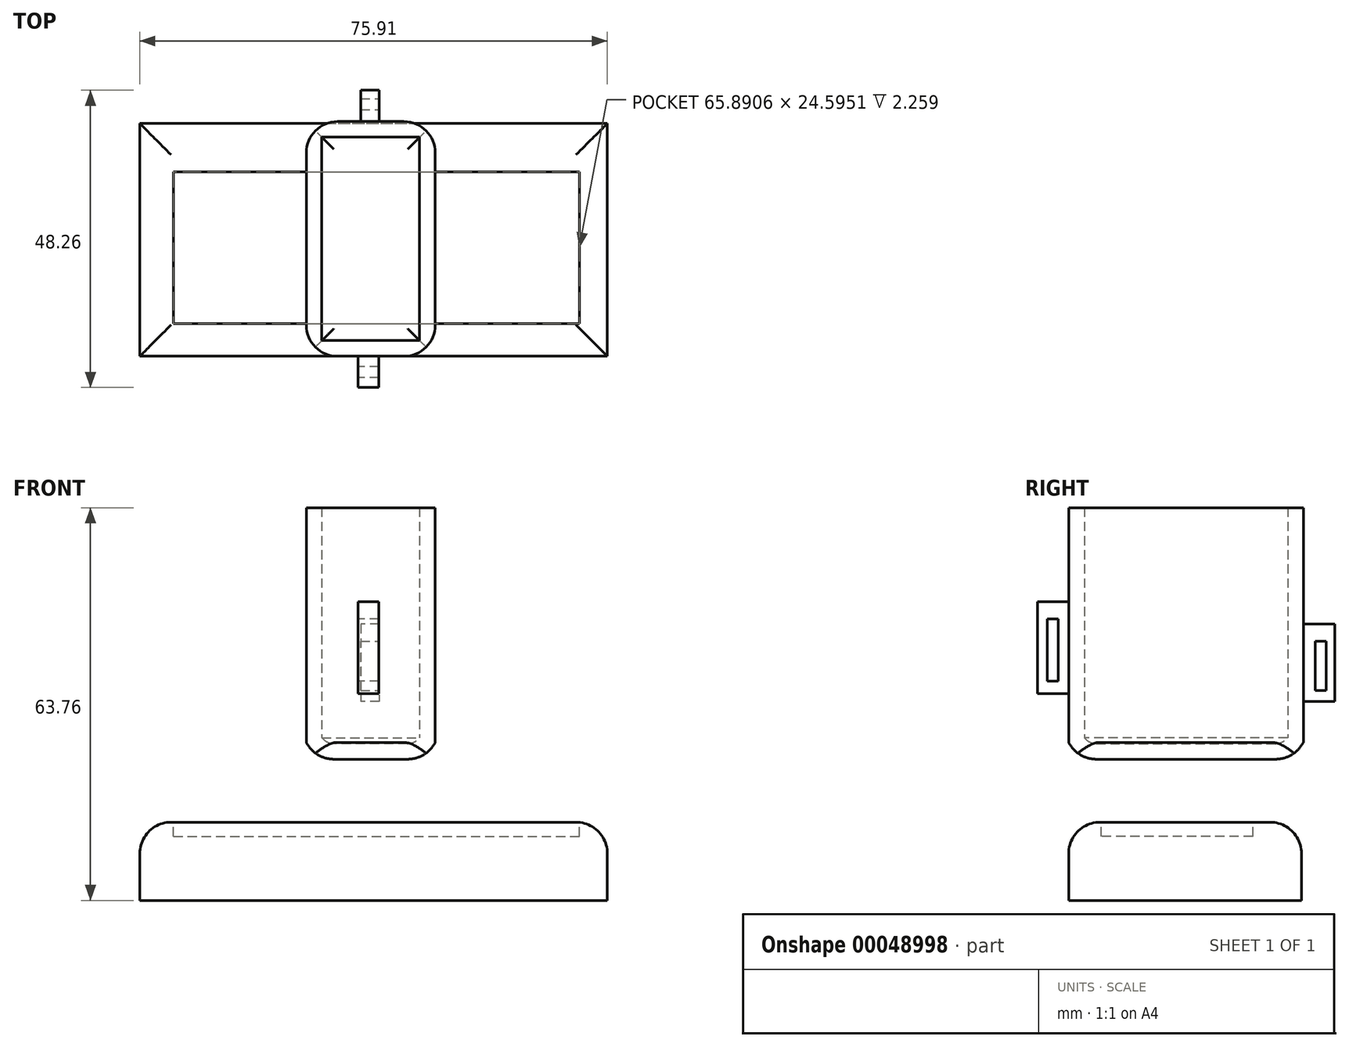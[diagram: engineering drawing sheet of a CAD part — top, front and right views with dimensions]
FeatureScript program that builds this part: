
annotation { "Feature Type Name" : "Feature", "Feature Type Description" : "" }
export const myFeature = defineFeature(function(context is Context, id is Id, definition is map)
    precondition{}
    {
        {
            var Q0;
            Q0=qCreatedBy(makeId("Top.planeOp"),FACE);
            var sketch = newSketch(context, id + "F0", { "sketchPlane" : qUnion([Q0])});
            skLineSegment(sketch, "E0.bottom", {"start": v(0, 0) * mm, "end": v(75.91, 0) * mm});
            skLineSegment(sketch, "E0.top", {"start": v(0, 37.8) * mm, "end": v(75.91, 37.8) * mm});
            skLineSegment(sketch, "E0.left", {"start": v(0, 0) * mm, "end": v(0, 37.8) * mm});
            skLineSegment(sketch, "E0.right", {"start": v(75.91, 0) * mm, "end": v(75.91, 37.8) * mm});
            skSolve(sketch);
        }
        {
            var Q0;
            Q0=makeQuery(id+"F0.imprint","IMPRINT",FACE,{"disambiguationData":[TD([[makeQuery(id+"F0.imprint","IMPRINT",EDGE,{"derivedFrom":sQuery(id+"F0.wireOp",EDGE,"E0.bottom")}),1.0]])]});
            extrude(context, id + "F1", {"entities" : qUnion([Q0]), "depth" : 12.7 * mm});
        }
        {
            var Q0;
            Q0=makeQuery(id+"F1.opExtrude","CAP_FACE",FACE,{"disambiguationData":[OSD([sQuery(id+"F0.wireOp",EDGE,"E0.bottom"),sQuery(id+"F0.wireOp",EDGE,"E0.top"),sQuery(id+"F0.wireOp",EDGE,"E0.left"),sQuery(id+"F0.wireOp",EDGE,"E0.right")])],"isStart":false});
            var sketch = newSketch(context, id + "F2", { "sketchPlane" : qUnion([Q0])});
            skLineSegment(sketch, "E1.bottom", {"start": v(5.47, 29.9) * mm, "end": v(71.36, 29.9) * mm});
            skLineSegment(sketch, "E1.top", {"start": v(5.47, 5.31) * mm, "end": v(71.36, 5.31) * mm});
            skLineSegment(sketch, "E1.left", {"start": v(5.47, 29.9) * mm, "end": v(5.47, 5.31) * mm});
            skLineSegment(sketch, "E1.right", {"start": v(71.36, 29.9) * mm, "end": v(71.36, 5.31) * mm});
            skSolve(sketch);
        }
        {
            var Q0;
            Q0=makeQuery(id+"F2.imprint","IMPRINT",FACE,{"disambiguationData":[TD([[makeQuery(id+"F2.imprint","IMPRINT",EDGE,{"derivedFrom":sQuery(id+"F2.wireOp",EDGE,"E1.bottom")}),-1.0]])]});
            extrude(context, id + "F3", {"entities" : qUnion([Q0]), "operationType" : NewBodyOperationType.REMOVE, "oppositeDirection" : true, "depth" : 2.3 * mm});
        }
        {
            var Q0;
            Q0=makeQuery(id+"F3.boolean.opBoolean","COPY",FACE,{"derivedFrom":makeQuery(id+"F3.opExtrude","CAP_FACE",FACE,{"disambiguationData":[OSD([sQuery(id+"F2.wireOp",EDGE,"E1.bottom"),sQuery(id+"F2.wireOp",EDGE,"E1.top"),sQuery(id+"F2.wireOp",EDGE,"E1.left"),sQuery(id+"F2.wireOp",EDGE,"E1.right")])],"isStart":false})});
            var sketch = newSketch(context, id + "F4", { "sketchPlane" : qUnion([Q0])});
            skSolve(sketch);
        }
        {
            var Q0;
            Q0=makeQuery(id+"F4.imprint","IMPRINT",FACE,{"disambiguationData":[TD([[makeQuery(id+"F4.imprint","IMPRINT",EDGE,{"derivedFrom":makeQuery(id+"F3.boolean.opBoolean","COPY",EDGE,{"derivedFrom":makeQuery(id+"F3.opExtrude","CAP_EDGE",EDGE,{"disambiguationData":[OSD([sQuery(id+"F2.wireOp",EDGE,"E1.bottom")])],"isStart":false})})}),-1.0]])]});
            var sketch = newSketch(context, id + "F5", { "sketchPlane" : qUnion([Q0])});
            skCircle(sketch, "E2", {"center": v(37.65, 17.16) * mm, "radius": 6.68 * mm});
            skSolve(sketch);
        }
        {
            var Q0;
            Q0=sQuery(id+"F5.wireOp",EDGE,"E2");
            extrude(context, id + "F6", {"bodyType" : ToolBodyType.SURFACE, "surfaceEntities" : qUnion([Q0]), "depth" : 12.7 * mm});
        }
        {
            var Q0;
            Q0=makeQuery(id+"F1.opExtrude","CAP_EDGE",EDGE,{"disambiguationData":[OSD([sQuery(id+"F0.wireOp",EDGE,"E0.bottom")])],"isStart":false});
            var Q1;
            Q1=makeQuery(id+"F1.opExtrude","CAP_EDGE",EDGE,{"disambiguationData":[OSD([sQuery(id+"F0.wireOp",EDGE,"E0.left")])],"isStart":false});
            var Q2;
            Q2=makeQuery(id+"F1.opExtrude","CAP_EDGE",EDGE,{"disambiguationData":[OSD([sQuery(id+"F0.wireOp",EDGE,"E0.right")])],"isStart":false});
            var Q3;
            Q3=makeQuery(id+"F1.opExtrude","CAP_EDGE",EDGE,{"disambiguationData":[OSD([sQuery(id+"F0.wireOp",EDGE,"E0.top")])],"isStart":false});
            fillet(context, id + "F7", {"entities" : qUnion([Q0, Q1, Q2, Q3]), "radius" : 5.08 * mm, "tangentPropagation" : true, "allowEdgeOverflow" : false});
        }
        {
            var Q0;
            Q0=qCreatedBy(makeId("Front.planeOp"),FACE);
            var sketch = newSketch(context, id + "F8", { "sketchPlane" : qUnion([Q0])});
            skLineSegment(sketch, "E3.bottom", {"start": v(27.02, 25.66) * mm, "end": v(47.98, 25.66) * mm});
            skLineSegment(sketch, "E3.top", {"start": v(27.02, 22.93) * mm, "end": v(47.98, 22.93) * mm});
            skLineSegment(sketch, "E3.left", {"start": v(27.02, 25.66) * mm, "end": v(27.02, 22.93) * mm});
            skLineSegment(sketch, "E3.right", {"start": v(47.98, 25.66) * mm, "end": v(47.98, 22.93) * mm});
            skSolve(sketch);
        }
        {
            var Q0;
            Q0=makeQuery(id+"F8.imprint","IMPRINT",FACE,{"disambiguationData":[TD([[makeQuery(id+"F8.imprint","IMPRINT",EDGE,{"derivedFrom":sQuery(id+"F8.wireOp",EDGE,"E3.bottom")}),-1.0]])]});
            extrude(context, id + "F9", {"entities" : qUnion([Q0]), "oppositeDirection" : true, "depth" : 38.1 * mm});
        }
        {
            var Q0;
            Q0=makeQuery(id+"F9.opExtrude","CAP_EDGE",EDGE,{"disambiguationData":[OSD([sQuery(id+"F8.wireOp",EDGE,"E3.top")])],"isStart":true});
            var Q1;
            Q1=makeQuery(id+"F9.opExtrude","SWEPT_EDGE",EDGE,{"disambiguationData":[OSD([sQuery(id+"F8.wireOp",EDGE,"E3.top"),sQuery(id+"F8.wireOp",EDGE,"E3.right")])]});
            var Q2;
            Q2=makeQuery(id+"F9.opExtrude","CAP_EDGE",EDGE,{"disambiguationData":[OSD([sQuery(id+"F8.wireOp",EDGE,"E3.top")])],"isStart":false});
            var Q3;
            Q3=makeQuery(id+"F9.opExtrude","SWEPT_EDGE",EDGE,{"disambiguationData":[OSD([sQuery(id+"F8.wireOp",EDGE,"E3.top"),sQuery(id+"F8.wireOp",EDGE,"E3.left")])]});
            fillet(context, id + "F10", {"entities" : qUnion([Q0, Q1, Q2, Q3]), "radius" : 5.08 * mm, "tangentPropagation" : true, "allowEdgeOverflow" : false});
        }
        {
            var Q0;
            Q0=makeQuery(id+"F9.opExtrude","SWEPT_FACE",FACE,{"disambiguationData":[OSD([sQuery(id+"F8.wireOp",EDGE,"E3.bottom")])]});
            var sketch = newSketch(context, id + "F11", { "sketchPlane" : qUnion([Q0])});
            skLineSegment(sketch, "E4.bottom", {"start": v(27.02, 38.1) * mm, "end": v(47.98, 38.1) * mm});
            skLineSegment(sketch, "E4.top", {"start": v(27.02, 0) * mm, "end": v(47.98, 0) * mm});
            skLineSegment(sketch, "E4.left", {"start": v(27.02, 38.1) * mm, "end": v(27.02, 0) * mm});
            skLineSegment(sketch, "E4.right", {"start": v(47.98, 38.1) * mm, "end": v(47.98, 0) * mm});
            skSolve(sketch);
        }
        {
            var Q0;
            Q0=makeQuery(id+"F11.imprint","IMPRINT",FACE,{"disambiguationData":[TD([[makeQuery(id+"F11.imprint","IMPRINT",EDGE,{"derivedFrom":sQuery(id+"F11.wireOp",EDGE,"E4.bottom")}),-1.0]])]});
            extrude(context, id + "F12", {"entities" : qUnion([Q0]), "operationType" : NewBodyOperationType.ADD, "depth" : 38.1 * mm});
        }
        {
            var Q0;
            Q0=makeQuery(id+"F12.opExtrude","CAP_FACE",FACE,{"disambiguationData":[OSD([sQuery(id+"F11.wireOp",EDGE,"E4.bottom"),sQuery(id+"F11.wireOp",EDGE,"E4.top"),sQuery(id+"F11.wireOp",EDGE,"E4.left"),sQuery(id+"F11.wireOp",EDGE,"E4.right")])],"isStart":false});
            shell(context, id + "F13", {"entities" : qUnion([Q0]), "thickness" : 2.54 * mm});
        }
        {
            var Q0;
            Q0=makeQuery(id+"F12.opExtrude","SWEPT_EDGE",EDGE,{"disambiguationData":[OSD([sQuery(id+"F11.wireOp",EDGE,"E4.bottom"),sQuery(id+"F11.wireOp",EDGE,"E4.right")])]});
            var Q1;
            Q1=makeQuery(id+"F12.opExtrude","SWEPT_EDGE",EDGE,{"disambiguationData":[OSD([sQuery(id+"F11.wireOp",EDGE,"E4.top"),sQuery(id+"F11.wireOp",EDGE,"E4.right")])]});
            var Q2;
            Q2=makeQuery(id+"F12.opExtrude","SWEPT_EDGE",EDGE,{"disambiguationData":[OSD([sQuery(id+"F11.wireOp",EDGE,"E4.bottom"),sQuery(id+"F11.wireOp",EDGE,"E4.left")])]});
            fillet(context, id + "F14", {"entities" : qUnion([Q0, Q1, Q2]), "radius" : 5.08 * mm, "tangentPropagation" : true, "allowEdgeOverflow" : false});
        }
        {
            var Q0;
            Q0=makeQuery(id+"F12.opExtrude","SWEPT_EDGE",EDGE,{"disambiguationData":[OSD([sQuery(id+"F11.wireOp",EDGE,"E4.top"),sQuery(id+"F11.wireOp",EDGE,"E4.left")])]});
            fillet(context, id + "F15", {"entities" : qUnion([Q0]), "radius" : 5.08 * mm, "tangentPropagation" : true, "allowEdgeOverflow" : false});
        }
        {
            var Q0;
            Q0=makeQuery(id+"F12.opExtrude","SWEPT_FACE",FACE,{"disambiguationData":[OSD([sQuery(id+"F11.wireOp",EDGE,"E4.top")])]});
            var sketch = newSketch(context, id + "F16", { "sketchPlane" : qUnion([Q0])});
            skLineSegment(sketch, "E5.bottom", {"start": v(35.47, 48.52) * mm, "end": v(38.81, 48.52) * mm});
            skLineSegment(sketch, "E5.top", {"start": v(35.47, 33.55) * mm, "end": v(38.81, 33.55) * mm});
            skLineSegment(sketch, "E5.left", {"start": v(35.47, 48.52) * mm, "end": v(35.47, 33.55) * mm});
            skLineSegment(sketch, "E5.right", {"start": v(38.81, 48.52) * mm, "end": v(38.81, 33.55) * mm});
            skSolve(sketch);
        }
        {
            var Q0;
            Q0=makeQuery(id+"F16.imprint","IMPRINT",FACE,{"disambiguationData":[TD([[makeQuery(id+"F16.imprint","IMPRINT",EDGE,{"derivedFrom":sQuery(id+"F16.wireOp",EDGE,"E5.bottom")}),-1.0]])]});
            extrude(context, id + "F17", {"entities" : qUnion([Q0]), "operationType" : NewBodyOperationType.ADD, "depth" : 5.08 * mm});
        }
        {
            var Q0;
            Q0=makeQuery(id+"F17.opExtrude","SWEPT_FACE",FACE,{"disambiguationData":[OSD([sQuery(id+"F16.wireOp",EDGE,"E5.left")])]});
            var sketch = newSketch(context, id + "F18", { "sketchPlane" : qUnion([Q0])});
            skLineSegment(sketch, "E6.bottom", {"start": v(1.66, 45.7) * mm, "end": v(3.47, 45.7) * mm});
            skLineSegment(sketch, "E6.top", {"start": v(1.66, 35.57) * mm, "end": v(3.47, 35.57) * mm});
            skLineSegment(sketch, "E6.left", {"start": v(1.66, 45.7) * mm, "end": v(1.66, 35.57) * mm});
            skLineSegment(sketch, "E6.right", {"start": v(3.47, 45.7) * mm, "end": v(3.47, 35.57) * mm});
            skSolve(sketch);
        }
        {
            var Q0;
            Q0=makeQuery(id+"F18.imprint","IMPRINT",FACE,{"disambiguationData":[TD([[makeQuery(id+"F18.imprint","IMPRINT",EDGE,{"derivedFrom":sQuery(id+"F18.wireOp",EDGE,"E6.bottom")}),-1.0]])]});
            extrude(context, id + "F19", {"entities" : qUnion([Q0]), "operationType" : NewBodyOperationType.REMOVE, "oppositeDirection" : true, "depth" : 5.08 * mm});
        }
        {
            var Q0;
            Q0=makeQuery(id+"F12.opExtrude","SWEPT_FACE",FACE,{"disambiguationData":[OSD([sQuery(id+"F11.wireOp",EDGE,"E4.bottom")])]});
            var sketch = newSketch(context, id + "F20", { "sketchPlane" : qUnion([Q0])});
            skLineSegment(sketch, "E7.bottom", {"start": v(-38.9, 44.85) * mm, "end": v(-35.87, 44.85) * mm});
            skLineSegment(sketch, "E7.top", {"start": v(-38.9, 32.32) * mm, "end": v(-35.87, 32.32) * mm});
            skLineSegment(sketch, "E7.left", {"start": v(-38.9, 44.85) * mm, "end": v(-38.9, 32.32) * mm});
            skLineSegment(sketch, "E7.right", {"start": v(-35.87, 44.85) * mm, "end": v(-35.87, 32.32) * mm});
            skSolve(sketch);
        }
        {
            var Q0;
            Q0=makeQuery(id+"F20.imprint","IMPRINT",FACE,{"disambiguationData":[TD([[makeQuery(id+"F20.imprint","IMPRINT",EDGE,{"derivedFrom":sQuery(id+"F20.wireOp",EDGE,"E7.bottom")}),-1.0]])]});
            extrude(context, id + "F21", {"entities" : qUnion([Q0]), "operationType" : NewBodyOperationType.ADD, "depth" : 5.08 * mm});
        }
        {
            var Q0;
            Q0=makeQuery(id+"F21.opExtrude","SWEPT_FACE",FACE,{"disambiguationData":[OSD([sQuery(id+"F20.wireOp",EDGE,"E7.left")])]});
            var sketch = newSketch(context, id + "F22", { "sketchPlane" : qUnion([Q0])});
            skLineSegment(sketch, "E8.bottom", {"start": v(40.02, 42.1) * mm, "end": v(41.84, 42.1) * mm});
            skLineSegment(sketch, "E8.top", {"start": v(40.02, 34.1) * mm, "end": v(41.84, 34.1) * mm});
            skLineSegment(sketch, "E8.left", {"start": v(40.02, 42.1) * mm, "end": v(40.02, 34.1) * mm});
            skLineSegment(sketch, "E8.right", {"start": v(41.84, 42.1) * mm, "end": v(41.84, 34.1) * mm});
            skSolve(sketch);
        }
        {
            var Q0;
            Q0=makeQuery(id+"F22.imprint","IMPRINT",FACE,{"disambiguationData":[TD([[makeQuery(id+"F22.imprint","IMPRINT",EDGE,{"derivedFrom":sQuery(id+"F22.wireOp",EDGE,"E8.bottom")}),-1.0]])]});
            extrude(context, id + "F23", {"entities" : qUnion([Q0]), "operationType" : NewBodyOperationType.REMOVE, "oppositeDirection" : true, "depth" : 5.08 * mm});
        }
    });
